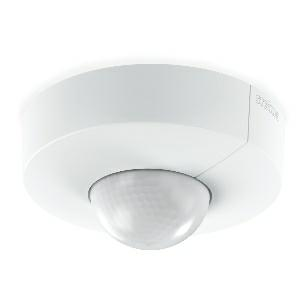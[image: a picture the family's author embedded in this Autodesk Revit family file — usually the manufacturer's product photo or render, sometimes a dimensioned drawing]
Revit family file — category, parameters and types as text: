
# Revit family: is_345_033828
name_source: partatom
category: Elektroinstallationen
revit_build: Autodesk Revit 2016 (Build: 20190508_0715(x64)
units: mm (PartAtom-declared; Revit-internal decimal feet)

## family parameters
Basisbauteil = Fläche
Beim Laden mit Abzugskörper schneiden = Nein
Bemaßung runder Anschluss = Durchmesser verwenden
Beschriftungsausrichtung beibehalten = Nein
Gemeinsam genutzt = Nein
Raumberechnungspunkt = Nein
Teiletyp = Normal

## types (1)
- IS 345
    Apparent Load = 0 VA
    Beschreibung = Type: Motion detectors; Dimensions (Ø x H): 126 x 65 mm; Mains power supply: 220 – 240 V / 50 – 60 Hz; Sensor Technology: passive infrared; Application, place: Outdoors, Indoors; Application, room: corridor / aisle, multi-storey / underground car park, outdoors, Indoors; Installation site: ceiling; Installation: Surface wiring; Switching zones: 280 switching zones; Electronic scalability: No; Mechanical scalability: No; Mounting height: 2,50 – 5,00 m; Optimum mounting height: 2,8 m; Detection angle: 360 °; Angle of aperture: 45 °; Sneak-by guard: Yes; Capability of masking out individual segments: Yes; Reach, radial: 12 x 6 m (72 m²); Reach, tangential: 23 x 6 m (138 m²); Twilight setting TEACH: Yes; Twilight setting: 2 – 1000 lx; Time setting: 5 sec – 15 min; Constant-lighting control: No; Basic light level function: No; Functions: Normal / test mode, Manual ON / ON-OFF; Settings via: Remote control, Potentiometers, Smart Remote; With remote control: No; Interconnection: Yes; IP-rating: IP54; Material: Plastic; Ambient temperature: -20 – 50 °C; Colour: white; Colour, RAL: 9003; Manufacturer's Warranty: 5 years; Version: PF - surface, rd.; PU1, EAN: 4007841033828
    Height = 0 mm  [stored 0 ft]
    Hersteller = Steinel
    Length = 126 mm
    Maximum range = 11.589 m
    ModVariant = Nein
    Modell = 033828
    Mounting Place = Ceiling
    Mounting Type = Surface mounted
    Number of Poles = 1
    OnlyDefault = Ja
    Power Factor = 1
    Product Name = IS 345
    Product group = Sensor-switched outdoor light
    ProductGroupID = 3
    Protection Class = Protection class
    Protection Degree = IP 54
    RlxData = <blob elided: 156181 chars, md5=64982aec>
    Sensor characteristics = Stretched
    Sensor type = Passive (infrared)
    SensorDataFile = <blob elided: 5885 chars, md5=98bccc25>
    Type of entry = Motion
    Typenbild = produkt1_033828.jpg
    Typenkommentare = Product without accessories
    URL = http://relux.com
    VarID = ---
    Voltage = 0 V
    Vorgabe-Ansicht = 1800 mm
    Weight = 0.00 kg
    Width = 0 mm  [stored 0 ft]

note: [stored X ft] marks values corroborated as IEEE doubles in the binary element streams (Revit-internal decimal feet)

## geometry (parser evidence)
native form markers: Blend x4, Sweep x17
no freeform markers — native parametric forms only
